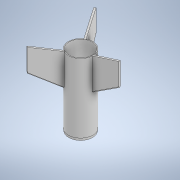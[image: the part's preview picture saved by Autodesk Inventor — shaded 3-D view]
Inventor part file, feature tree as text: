
AUTODESK INVENTOR PART (.ipt)
format: ipt  version: 2020.3 (Build 243373000, 373)  size: 275,968 bytes
history: native  units: mm
features: extrude x6, sketch x5, plane x2, chamfer x2, projected_geometry x2, pattern_circular x1, split x1
ambient origin geometry x8: Origin, YZ Plane, XZ Plane, XY Plane, X Axis, Y Axis, Z Axis, Center Point
bodies: Solid1 (feature_tree), Solid2 (feature_tree), Solid3 (feature_tree)
feature tree (19):
  sketch  "Sketch1"  dims[d0=50.0mm d1=51.8mm]
  extrude  "Extrusion1"  Depth=51.8mm
  extrude  "Extrusion2"  Depth=75.0mm TaperAngle=0.0deg
  extrude  "Extrusion4"  Depth=70.0mm
  plane  "Work Plane1"
  extrude  "Extrusion5"  Depth=50.0mm
  chamfer  "Chamfer1"  Distance=3.6mm
  chamfer  "Chamfer2"  Distance=175.0mm
  pattern_circular  "Circular Pattern3"  [2 undecoded]
  plane  "Work Plane2"
  split  "Split1"
  extrude  "Extrusion6"  [1 undecoded]
  extrude  "Extrusion7"  Depth=5.0mm TaperAngle=45.0deg
  sketch  "Sketch4"  dims[d2=53.6mm d3=75.0mm d4=180.0mm d5=0.0mm d6=0.0mm]
  projected_geometry  "Projected Loop1"
  sketch  "Sketch7"  dims[d21=9.930923mm d24=50.0mm]
  sketch  "Sketch8"  dims[d25=60.0mm d26=3.6mm d27=0.0mm d31=175.0mm d32=0.0mm d33=5.0mm d34=-145.0mm d35=50.0mm d36=51.8mm d37=53.6mm d38=5.0mm d39=5.0mm d40=0.0mm d41=1.8mm d42=2.0mm d43=45.0deg d44=1.8mm d45=2.0mm d46=45.0deg d47=30.0mm d48=360.0deg d50=-75.0mm d51=50.0mm d52=51.8mm d53=5.0mm d54=0.0mm d55=50.0mm d56=51.8mm d57=5.0mm d58=0.0mm d11=0.5mm d12=0.872665mm d13=0.5mm d14=0.872665mm]
  projected_geometry  "Project Cut Edges1"
  sketch  "Sketch5"  dims[d7=75.0mm d8=0.0mm d18=70.0mm]
note: 3 required parameter values undecoded (feature->parameter linkage not recoverable at this tier; creation-order binding heuristic only, values carry confidence <= 0.55)
